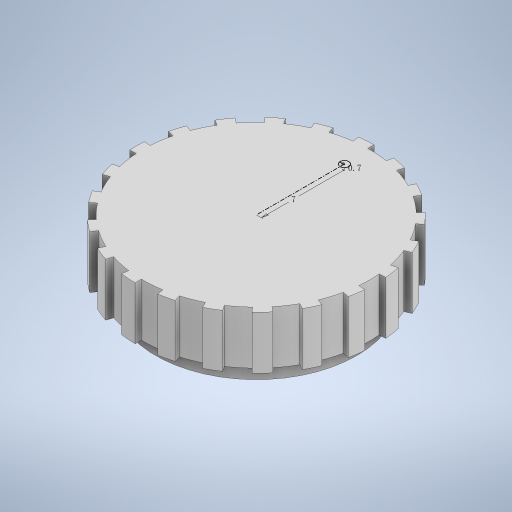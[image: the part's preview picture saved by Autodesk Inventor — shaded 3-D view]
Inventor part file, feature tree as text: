
AUTODESK INVENTOR PART (.ipt)
format: ipt  version: 2023 (Build 270158000, 158)  size: 424,960 bytes
history: native  units: mm
features: sketch x8, extrude x5
ambient origin geometry x8: Origin, YZ Plane, XZ Plane, XY Plane, X Axis, Y Axis, Z Axis, Center Point
bodies: 实体1 (feature_tree)
feature tree (13):
  extrude  "拉伸1"  Depth=2.1mm
  extrude  "拉伸2"  Depth=2.3mm TaperAngle=0.0deg
  sketch  "草图5"  dims[d5=0.4mm d6=0.0mm d27=0.7mm]
  extrude  "拉伸7"  Depth=0.4mm
  extrude  "拉伸6"  Depth=7.0mm
  sketch  "草图7"  dims[d32=1.22173mm d33=210.0mm d35=360.0deg]
  sketch  "草图8"  dims[d37=0.4mm d38=0.0mm]
  extrude  "拉伸8"  Depth=210.0mm TaperAngle=360.0deg
  sketch  "草图1"  dims[d0=3.2mm d1=2.1mm]
  sketch  "草图2"  dims[d2=18.0mm d3=2.3mm d4=0.0mm]
  sketch  "草图6"  dims[d28=7.0mm d31=0.5mm]
  sketch  "草图9"  dims[d39=14.0mm]
  sketch  "草图10"  dims[d40=3.0mm d41=0.0mm d42=1.0mm d43=1.5mm d44=0.0mm]
